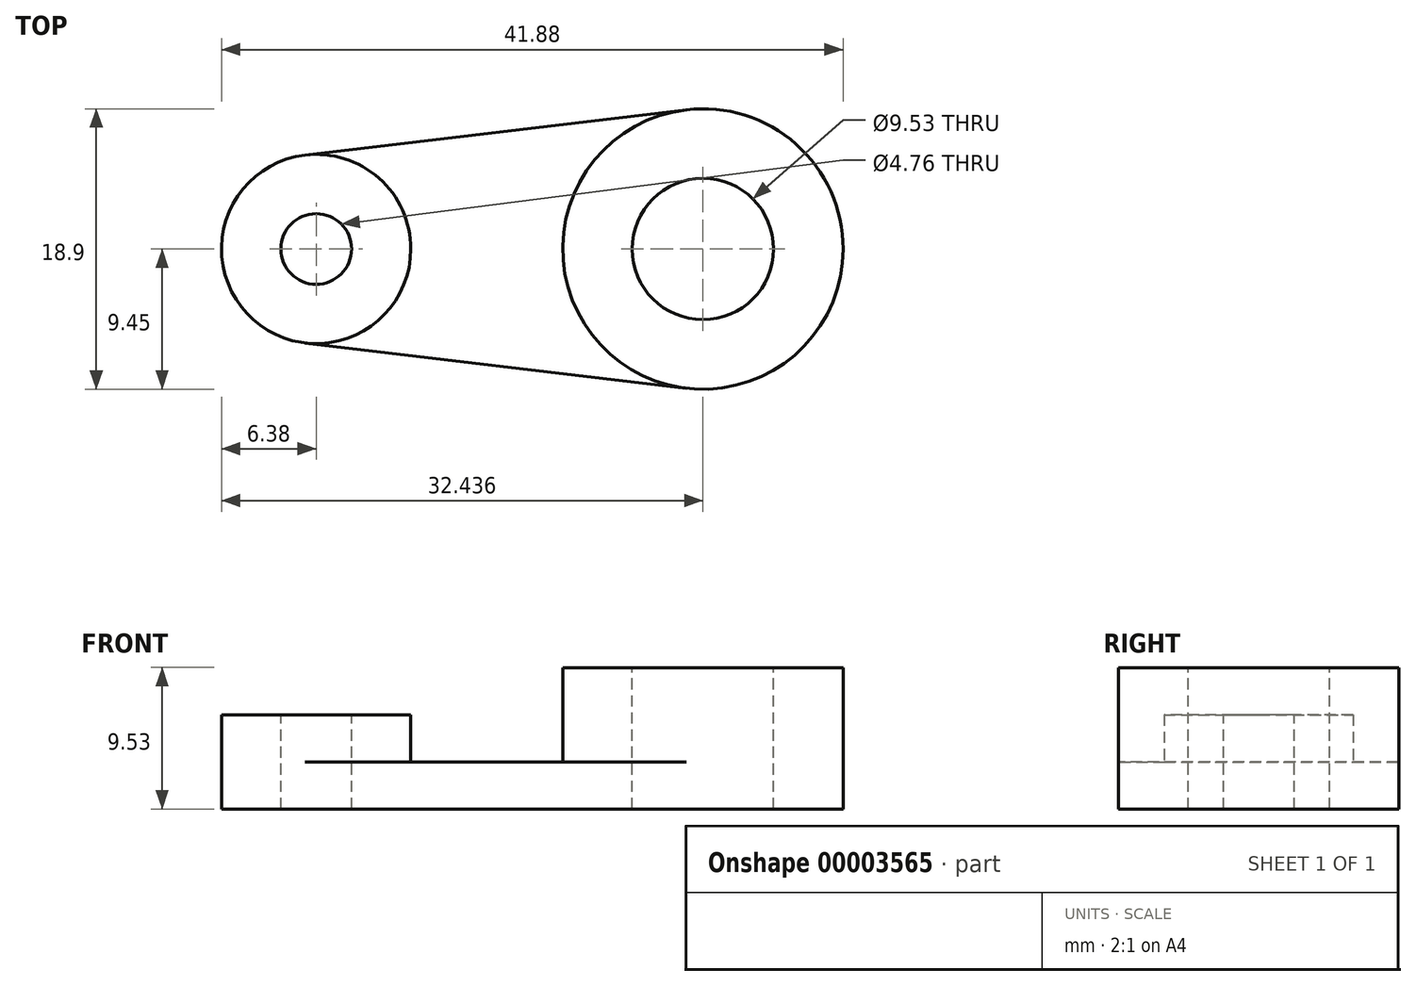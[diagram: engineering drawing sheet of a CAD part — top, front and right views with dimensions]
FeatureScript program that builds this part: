
annotation { "Feature Type Name" : "Feature", "Feature Type Description" : "" }
export const myFeature = defineFeature(function(context is Context, id is Id, definition is map)
    precondition{}
    {
        {
            var Q0;
            Q0=qCreatedBy(makeId("Top.planeOp"),FACE);
            var sketch = newSketch(context, id + "F0", { "sketchPlane" : qUnion([Q0])});
            skCircle(sketch, "E0", {"center": v(0, 0) * mm, "radius": 6.38 * mm});
            skLineSegment(sketch, "E1", {"start": v(0.66, 0) * mm, "end": v(26.06, 0) * mm, "construction": true});
            skSolve(sketch);
        }
        {
            var Q0;
            Q0 = qSketchRegion(id + "F0", true);
            extrude(context, id + "F1", {"entities" : qUnion([Q0]), "depth" : 6.35 * mm});
        }
        {
            var Q0;
            Q0=qCreatedBy(makeId("Top.planeOp"),FACE);
            var sketch = newSketch(context, id + "F2", { "sketchPlane" : qUnion([Q0])});
            skCircle(sketch, "E2", {"center": v(26.06, 0) * mm, "radius": 9.45 * mm});
            skSolve(sketch);
        }
        {
            var Q0;
            Q0=qCreatedBy(makeId("Top.planeOp"),FACE);
            var sketch = newSketch(context, id + "F3", { "sketchPlane" : qUnion([Q0])});
            skLineSegment(sketch, "E3", {"start": v(-0.75, 6.33) * mm, "end": v(24.94, 9.38) * mm});
            skLineSegment(sketch, "E4", {"start": v(24.94, 9.38) * mm, "end": v(24.94, -9.38) * mm});
            skLineSegment(sketch, "E5", {"start": v(24.94, -9.38) * mm, "end": v(-0.75, -6.33) * mm});
            skLineSegment(sketch, "E6", {"start": v(-0.75, -6.33) * mm, "end": v(-0.75, 6.33) * mm});
            skSolve(sketch);
        }
        {
            var Q0;
            Q0 = qSketchRegion(id + "F3", true);
            extrude(context, id + "F4", {"entities" : qUnion([Q0]), "operationType" : NewBodyOperationType.ADD, "depth" : 3.17 * mm});
        }
        {
            var Q0;
            Q0=makeQuery(id+"F2.imprint","IMPRINT",FACE,{"disambiguationData":[TD([[makeQuery(id+"F2.imprint","IMPRINT",EDGE,{"derivedFrom":sQuery(id+"F2.wireOp",EDGE,"E2")}),1.0]])]});
            extrude(context, id + "F5", {"entities" : qUnion([Q0]), "operationType" : NewBodyOperationType.ADD, "depth" : 9.52 * mm});
        }
        {
            var Q0;
            Q0=makeQuery(id+"F5.opExtrude","CAP_FACE",FACE,{"disambiguationData":[OSD([sQuery(id+"F2.wireOp",EDGE,"E2")])],"isStart":false});
            var sketch = newSketch(context, id + "F6", { "sketchPlane" : qUnion([Q0])});
            skCircle(sketch, "E7", {"center": v(0, 0) * mm, "radius": 2.38 * mm});
            skCircle(sketch, "E8", {"center": v(26.06, 0) * mm, "radius": 4.76 * mm});
            skSolve(sketch);
        }
        {
            var Q0;
            Q0 = qSketchRegion(id + "F6", true);
            extrude(context, id + "F7", {"entities" : qUnion([Q0]), "operationType" : NewBodyOperationType.REMOVE, "endBound" : BoundingType.THROUGH_ALL, "oppositeDirection" : true, "depth" : 25.4 * mm});
        }
    });
